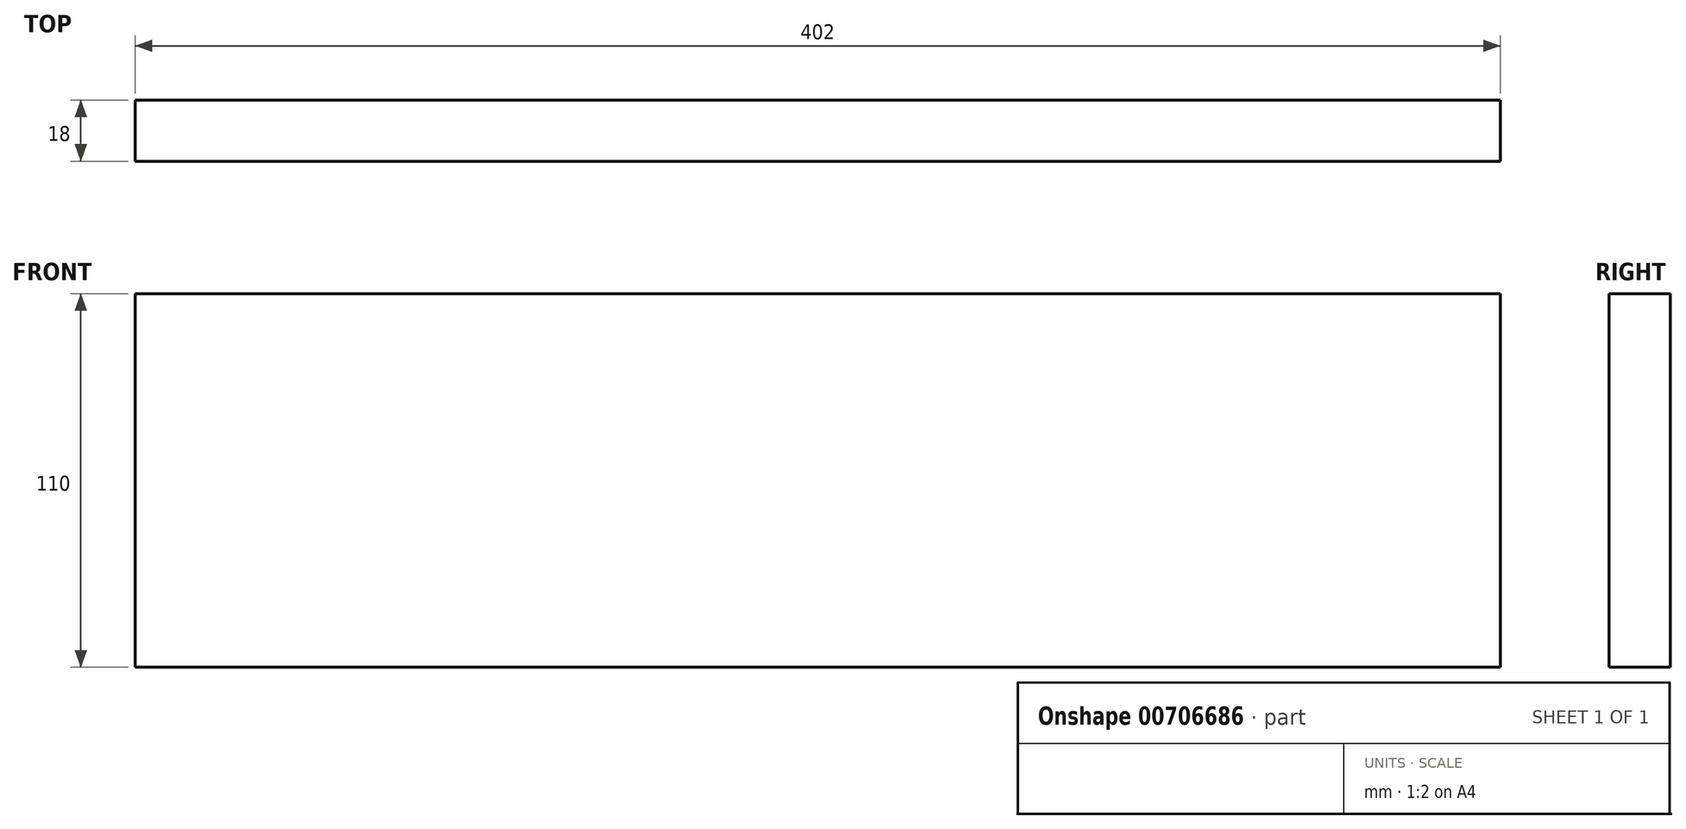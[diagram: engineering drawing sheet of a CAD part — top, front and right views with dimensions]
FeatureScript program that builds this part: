
annotation { "Feature Type Name" : "Feature", "Feature Type Description" : "" }
export const myFeature = defineFeature(function(context is Context, id is Id, definition is map)
    precondition{}
    {
        {
            var Q0;
            Q0=qCreatedBy(makeId("Front.planeOp"),FACE);
            var sketch = newSketch(context, id + "F0", { "sketchPlane" : qUnion([Q0])});
            skLineSegment(sketch, "E0.bottom", {"start": v(-201, -55) * mm, "end": v(201, -55) * mm});
            skLineSegment(sketch, "E0.top", {"start": v(-201, 55) * mm, "end": v(201, 55) * mm});
            skLineSegment(sketch, "E0.left", {"start": v(-201, -55) * mm, "end": v(-201, 55) * mm});
            skLineSegment(sketch, "E0.right", {"start": v(201, -55) * mm, "end": v(201, 55) * mm});
            skPoint(sketch, "E0.middle", {"position": v(0, 0) * mm});
            skSolve(sketch);
        }
        {
            var Q0;
            Q0=makeQuery(id+"F0.imprint","IMPRINT",FACE,{"disambiguationData":[TD([[makeQuery(id+"F0.imprint","IMPRINT",EDGE,{"derivedFrom":sQuery(id+"F0.wireOp",EDGE,"E0.bottom")}),1.0]])]});
            extrude(context, id + "F1", {"entities" : qUnion([Q0]), "depth" : 18 * mm, "offsetDistance" : 25 * mm, "symmetric" : true});
        }
    });
